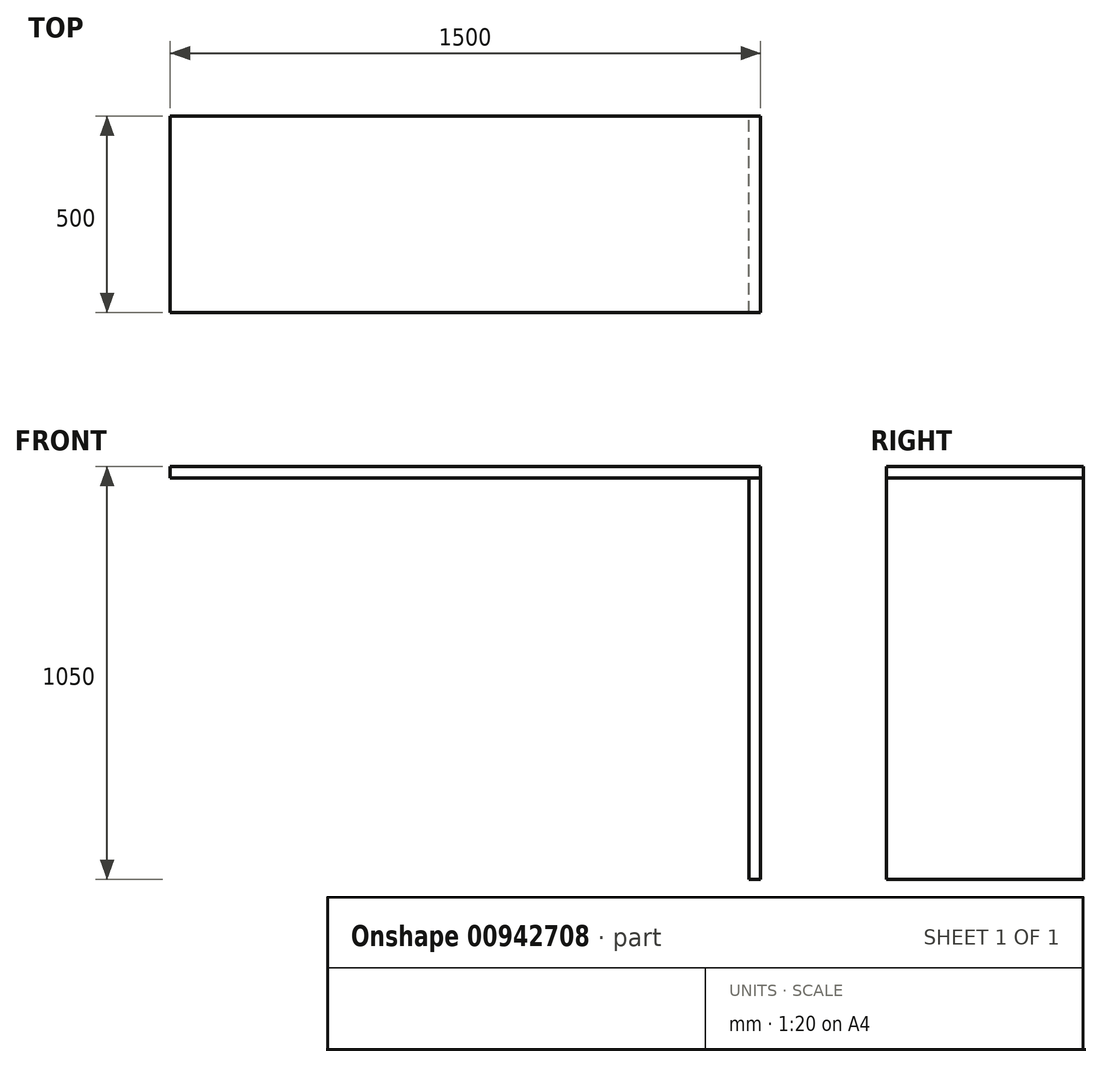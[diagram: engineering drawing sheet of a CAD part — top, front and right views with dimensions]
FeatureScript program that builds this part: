
annotation { "Feature Type Name" : "Feature", "Feature Type Description" : "" }
export const myFeature = defineFeature(function(context is Context, id is Id, definition is map)
    precondition{}
    {
        {
            var Q0;
            Q0=qCreatedBy(makeId("Top.planeOp"),FACE);
            var sketch = newSketch(context, id + "F0", { "sketchPlane" : qUnion([Q0])});
            skLineSegment(sketch, "E0.bottom", {"start": v(-750, -250) * mm, "end": v(750, -250) * mm});
            skLineSegment(sketch, "E0.top", {"start": v(-750, 250) * mm, "end": v(750, 250) * mm});
            skLineSegment(sketch, "E0.left", {"start": v(-750, 250) * mm, "end": v(-750, -250) * mm});
            skLineSegment(sketch, "E0.right", {"start": v(750, 250) * mm, "end": v(750, -250) * mm});
            skLineSegment(sketch, "E1", {"start": v(-750, 0) * mm, "end": v(0, 0) * mm, "construction": true});
            skLineSegment(sketch, "E2", {"start": v(0, 0) * mm, "end": v(750, 0) * mm, "construction": true});
            skLineSegment(sketch, "E3", {"start": v(0, 0) * mm, "end": v(0, 250) * mm, "construction": true});
            skLineSegment(sketch, "E4", {"start": v(0, 0) * mm, "end": v(0, -250) * mm, "construction": true});
            skSolve(sketch);
        }
        {
            var Q0;
            Q0=makeQuery(id+"F0.imprint","IMPRINT",FACE,{"disambiguationData":[TD([[makeQuery(id+"F0.imprint","IMPRINT",EDGE,{"derivedFrom":sQuery(id+"F0.wireOp",EDGE,"E0.bottom")}),1.0]])]});
            extrude(context, id + "F1", {"entities" : qUnion([Q0]), "depth" : 30 * mm, "offsetDistance" : 25 * mm});
        }
        {
            var Q0;
            Q0=makeQuery(id+"F1.opExtrude","SWEPT_FACE",FACE,{"disambiguationData":[OSD([sQuery(id+"F0.wireOp",EDGE,"E0.right")])]});
            var sketch = newSketch(context, id + "F2", { "sketchPlane" : qUnion([Q0])});
            skLineSegment(sketch, "E5", {"start": v(-250, -1020) * mm, "end": v(-250, 0) * mm});
            skLineSegment(sketch, "E6", {"start": v(250, -1020) * mm, "end": v(250, 0) * mm});
            skLineSegment(sketch, "E7", {"start": v(0, -547.67) * mm, "end": v(0, 0) * mm, "construction": true});
            skLineSegment(sketch, "E8", {"start": v(-250, 0) * mm, "end": v(250, 0) * mm});
            skLineSegment(sketch, "E9", {"start": v(-250, -1020) * mm, "end": v(250, -1020) * mm});
            skSolve(sketch);
        }
        {
            var Q0;
            Q0=makeQuery(id+"F2.imprint","IMPRINT",FACE,{"disambiguationData":[TD([[makeQuery(id+"F2.imprint","IMPRINT",EDGE,{"derivedFrom":sQuery(id+"F2.wireOp",EDGE,"E5")}),-1.0]])]});
            extrude(context, id + "F3", {"entities" : qUnion([Q0]), "oppositeDirection" : true, "depth" : 30 * mm, "offsetDistance" : 25 * mm});
        }
    });
